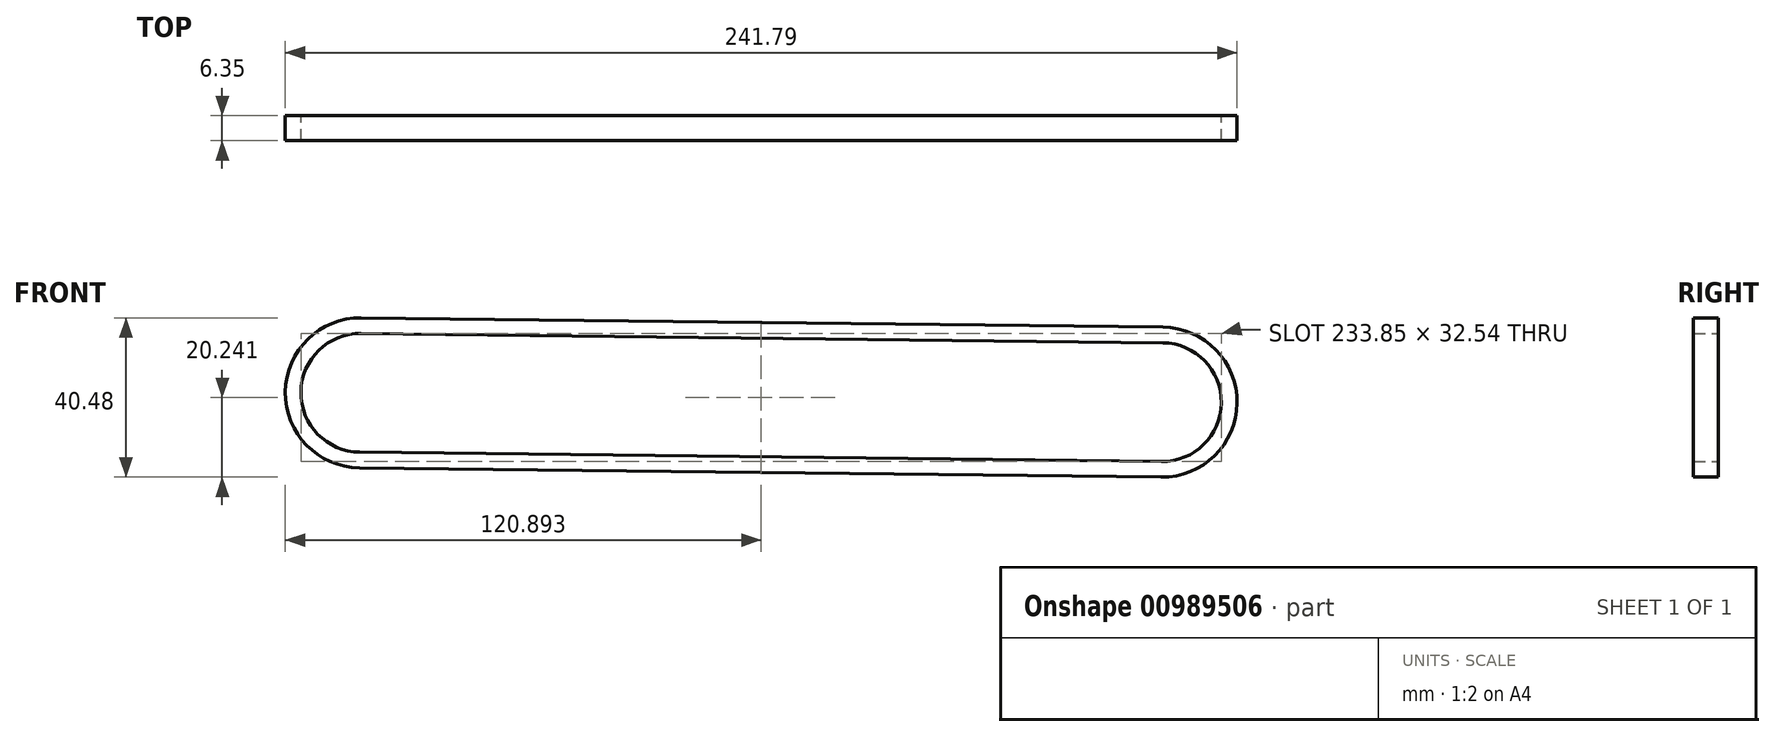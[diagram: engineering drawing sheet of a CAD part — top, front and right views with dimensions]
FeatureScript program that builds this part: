
annotation { "Feature Type Name" : "Feature", "Feature Type Description" : "" }
export const myFeature = defineFeature(function(context is Context, id is Id, definition is map)
    precondition{}
    {
        {
            var Q0;
            Q0=qCreatedBy(makeId("Front.planeOp"),FACE);
            var sketch = newSketch(context, id + "F0", { "sketchPlane" : qUnion([Q0])});
            skCircle(sketch, "E0", {"center": v(0, 0) * mm, "radius": 19.05 * mm, "construction": true});
            skCircle(sketch, "E1", {"center": v(-203.7, 2.38) * mm, "radius": 19.05 * mm, "construction": true});
            skLineSegment(sketch, "E2", {"start": v(-203.47, 21.43) * mm, "end": v(0.22, 19.05) * mm});
            skArc(sketch, "E3", {"start": v(-203.47, 21.43) * mm, "mid": v(-222.74, 2.6) * mm, "end": v(-203.92, -16.67) * mm});
            skLineSegment(sketch, "E4", {"start": v(-203.92, -16.67) * mm, "end": v(-0.22, -19.05) * mm});
            skArc(sketch, "E5", {"start": v(0.22, 19.05) * mm, "mid": v(19.05, -0.22) * mm, "end": v(-0.22, -19.05) * mm});
            skLineSegment(sketch, "E6", {"start": v(-203.7, 2.38) * mm, "end": v(0, 0) * mm, "construction": true});
            skArc(sketch, "E7.0.startCap", {"start": v(-203.87, -12.7) * mm, "mid": v(-218.77, 2.56) * mm, "end": v(-203.52, 17.46) * mm});
            skArc(sketch, "E7.0.endCap", {"start": v(0.18, 15.08) * mm, "mid": v(15.08, -0.18) * mm, "end": v(-0.18, -15.08) * mm});
            skLineSegment(sketch, "E7.0.left", {"start": v(-203.52, 17.46) * mm, "end": v(0.18, 15.08) * mm});
            skLineSegment(sketch, "E7.0.right", {"start": v(-203.87, -12.7) * mm, "end": v(-0.18, -15.08) * mm});
            skSolve(sketch);
        }
        {
            var Q0;
            Q0 = qSketchRegion(id + "F0", true);
            extrude(context, id + "F1", {"entities" : qUnion([Q0]), "depth" : 6.35 * mm, "offsetDistance" : 25.4 * mm});
        }
    });
